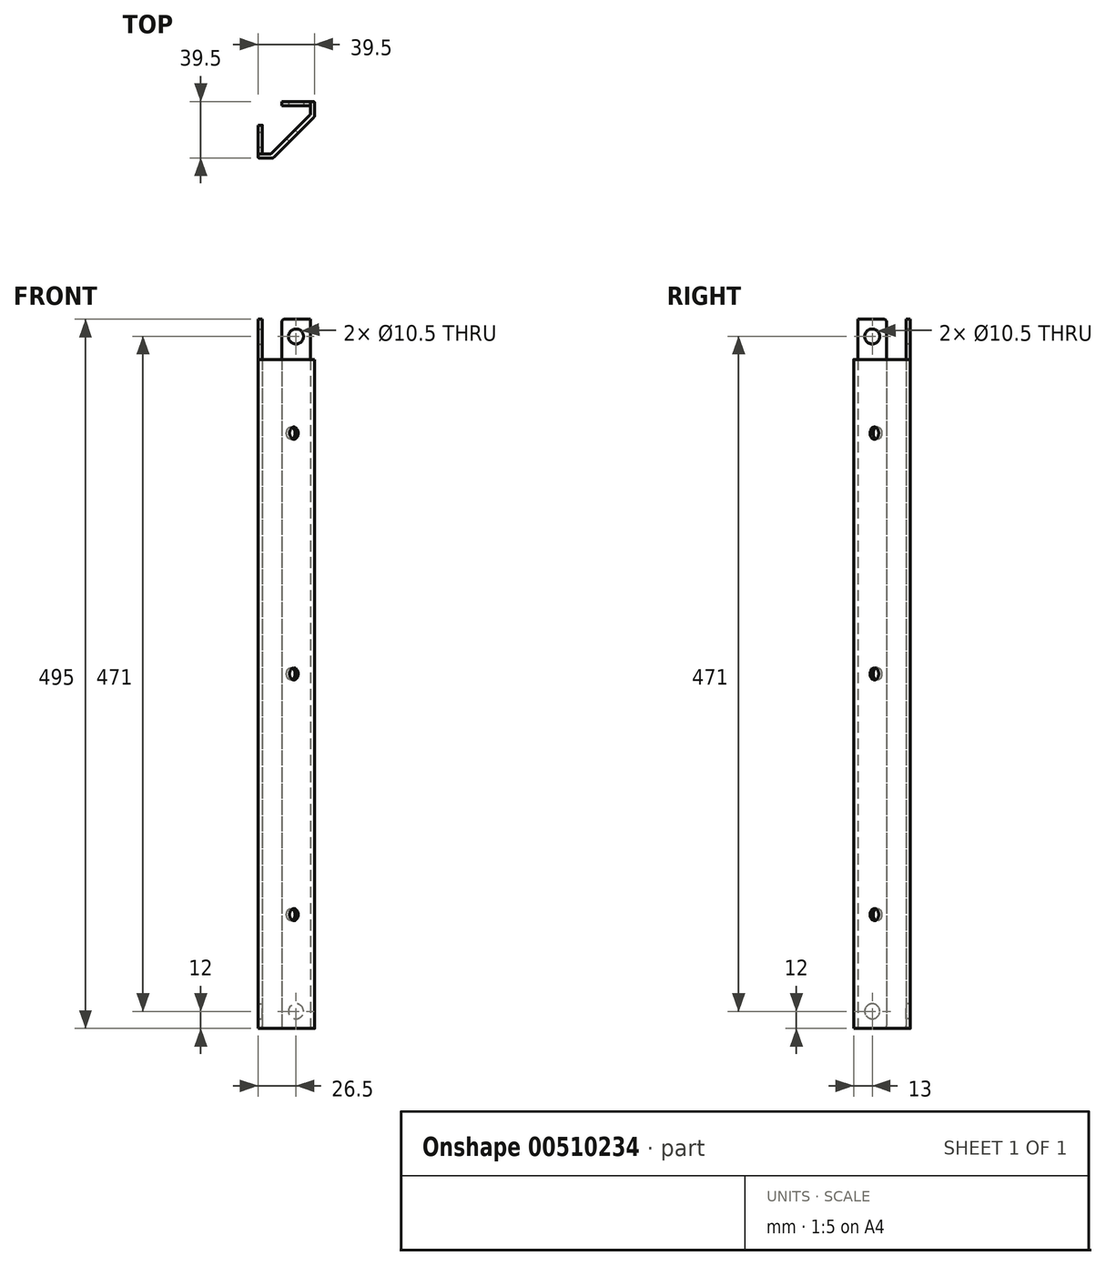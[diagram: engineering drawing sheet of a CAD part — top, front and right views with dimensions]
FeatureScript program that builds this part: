
annotation { "Feature Type Name" : "Feature", "Feature Type Description" : "" }
export const myFeature = defineFeature(function(context is Context, id is Id, definition is map)
    precondition{}
    {
        {
            var Q0;
            Q0=qCreatedBy(makeId("Top.planeOp"),FACE);
            var sketch = newSketch(context, id + "F0", { "sketchPlane" : qUnion([Q0])});
            skLineSegment(sketch, "E0", {"start": v(0, 53.87) * mm, "end": v(0, -58.58) * mm, "construction": true});
            skLineSegment(sketch, "E1", {"start": v(-55.23, 0) * mm, "end": v(53.75, 0) * mm, "construction": true});
            skLineSegment(sketch, "E2.bottom", {"start": v(-19.75, 19.75) * mm, "end": v(19.75, 19.75) * mm, "construction": true});
            skLineSegment(sketch, "E2.top", {"start": v(-19.75, -19.75) * mm, "end": v(19.75, -19.75) * mm, "construction": true});
            skLineSegment(sketch, "E2.left", {"start": v(-19.75, 19.75) * mm, "end": v(-19.75, -19.75) * mm, "construction": true});
            skLineSegment(sketch, "E2.right", {"start": v(19.75, 19.75) * mm, "end": v(19.75, -19.75) * mm, "construction": true});
            skLineSegment(sketch, "E3", {"start": v(-19.75, -19.75) * mm, "end": v(-19.75, 3.25) * mm});
            skLineSegment(sketch, "E4", {"start": v(-19.75, 3.25) * mm, "end": v(-16.75, 3.25) * mm});
            skLineSegment(sketch, "E5", {"start": v(-16.75, 3.25) * mm, "end": v(-16.75, -16.75) * mm});
            skLineSegment(sketch, "E6", {"start": v(-19.75, -19.75) * mm, "end": v(-9.25, -19.75) * mm});
            skLineSegment(sketch, "E7", {"start": v(-9.25, -19.75) * mm, "end": v(19.75, 9.25) * mm, "construction": true});
            skLineSegment(sketch, "E8", {"start": v(-16.75, -6.75) * mm, "end": v(-8.75, -6.75) * mm, "construction": true});
            skLineSegment(sketch, "E9", {"start": v(-8.75, -6.75) * mm, "end": v(-8.75, -15.25) * mm, "construction": true});
            skLineSegment(sketch, "E10.0", {"start": v(-10.5, -16.75) * mm, "end": v(16.75, 10.5) * mm});
            skLineSegment(sketch, "E11", {"start": v(-16.75, -16.75) * mm, "end": v(-10.5, -16.75) * mm});
            skLineSegment(sketch, "E12.0", {"start": v(-10.66, -18.34) * mm, "end": v(18.84, 11.16) * mm, "construction": true});
            skLineSegment(sketch, "E13", {"start": v(-9.25, -19.75) * mm, "end": v(19.75, 9.25) * mm});
            skLineSegment(sketch, "E14", {"start": v(19.75, 9.25) * mm, "end": v(19.75, 19.75) * mm});
            skLineSegment(sketch, "E15", {"start": v(19.75, 19.75) * mm, "end": v(-3.25, 19.75) * mm});
            skLineSegment(sketch, "E16", {"start": v(-3.25, 19.75) * mm, "end": v(-3.25, 16.75) * mm});
            skLineSegment(sketch, "E17", {"start": v(-3.25, 16.75) * mm, "end": v(16.75, 16.75) * mm});
            skLineSegment(sketch, "E18", {"start": v(16.75, 16.75) * mm, "end": v(16.75, 10.5) * mm});
            skSolve(sketch);
        }
        {
            var Q0;
            Q0=qSketchRegion(id+"F0",true);
            extrude(context, id + "F1", {"entities" : qUnion([Q0]), "depth" : 495 * mm, "symmetric" : true});
        }
        {
            var Q0;
            Q0=makeQuery(id+"F1.opExtrude","CAP_FACE",FACE,{"disambiguationData":[OSD([sQuery(id+"F0.wireOp",EDGE,"E3"),sQuery(id+"F0.wireOp",EDGE,"E4"),sQuery(id+"F0.wireOp",EDGE,"E5"),sQuery(id+"F0.wireOp",EDGE,"E6"),sQuery(id+"F0.wireOp",EDGE,"E10.0"),sQuery(id+"F0.wireOp",EDGE,"E11"),sQuery(id+"F0.wireOp",EDGE,"E13"),sQuery(id+"F0.wireOp",EDGE,"E14"),sQuery(id+"F0.wireOp",EDGE,"E15"),sQuery(id+"F0.wireOp",EDGE,"E16"),sQuery(id+"F0.wireOp",EDGE,"E17"),sQuery(id+"F0.wireOp",EDGE,"E18")])],"isStart":false});
            var sketch = newSketch(context, id + "F2", { "sketchPlane" : qUnion([Q0])});
            skLineSegment(sketch, "E19.0", {"start": v(-16.75, -16.75) * mm, "end": v(-10.5, -16.75) * mm});
            skLineSegment(sketch, "E19.1", {"start": v(-10.5, -16.75) * mm, "end": v(16.75, 10.5) * mm});
            skLineSegment(sketch, "E19.2", {"start": v(16.75, 16.75) * mm, "end": v(16.75, 10.5) * mm});
            skLineSegment(sketch, "E19.3", {"start": v(19.75, 9.25) * mm, "end": v(19.75, 19.75) * mm});
            skLineSegment(sketch, "E19.4", {"start": v(-9.25, -19.75) * mm, "end": v(19.75, 9.25) * mm});
            skLineSegment(sketch, "E19.5", {"start": v(-19.75, -19.75) * mm, "end": v(-9.25, -19.75) * mm});
            skLineSegment(sketch, "E20", {"start": v(-16.75, -16.75) * mm, "end": v(-19.75, -16.75) * mm});
            skLineSegment(sketch, "E21", {"start": v(-19.75, -16.75) * mm, "end": v(-19.75, -19.75) * mm});
            skLineSegment(sketch, "E22", {"start": v(16.75, 16.75) * mm, "end": v(16.75, 19.75) * mm});
            skLineSegment(sketch, "E23", {"start": v(16.75, 19.75) * mm, "end": v(19.75, 19.75) * mm});
            skSolve(sketch);
        }
        {
            var Q0;
            Q0=qSketchRegion(id+"F2",true);
            extrude(context, id + "F3", {"entities" : qUnion([Q0]), "operationType" : NewBodyOperationType.REMOVE, "oppositeDirection" : true, "depth" : 28 * mm});
        }
        {
            var Q0;
            Q0=makeQuery(id+"F1.opExtrude","SWEPT_FACE",FACE,{"disambiguationData":[OSD([sQuery(id+"F0.wireOp",EDGE,"E13")])]});
            var sketch = newSketch(context, id + "F4", { "sketchPlane" : qUnion([Q0])});
            skLineSegment(sketch, "E24", {"start": v(0, 219.5) * mm, "end": v(0, -219.5) * mm, "construction": true});
            skLineSegment(sketch, "E25", {"start": v(-20.5, 0) * mm, "end": v(20.5, 0) * mm, "construction": true});
            skCircle(sketch, "E26", {"center": v(0, 168) * mm, "radius": 4.25 * mm});
            skCircle(sketch, "E27.MirrorC", {"center": v(0, -168) * mm, "radius": 4.25 * mm});
            skCircle(sketch, "E28", {"center": v(0, 0) * mm, "radius": 4.25 * mm});
            skSolve(sketch);
        }
        {
            var Q0;
            Q0=qSketchRegion(id+"F4",true);
            extrude(context, id + "F5", {"entities" : qUnion([Q0]), "operationType" : NewBodyOperationType.REMOVE, "oppositeDirection" : true, "depth" : 25 * mm});
        }
        {
            var Q0;
            Q0=makeQuery(id+"F1.opExtrude","SWEPT_FACE",FACE,{"disambiguationData":[OSD([sQuery(id+"F0.wireOp",EDGE,"E5")])]});
            var sketch = newSketch(context, id + "F6", { "sketchPlane" : qUnion([Q0])});
            skLineSegment(sketch, "E29", {"start": v(-6.75, 247.5) * mm, "end": v(-6.75, -247.5) * mm, "construction": true});
            skCircle(sketch, "E30", {"center": v(-6.75, 235.5) * mm, "radius": 5.25 * mm});
            skCircle(sketch, "E31", {"center": v(-6.75, -235.5) * mm, "radius": 5.25 * mm});
            skSolve(sketch);
        }
        {
            var Q0;
            Q0=qSketchRegion(id+"F6",true);
            extrude(context, id + "F7", {"entities" : qUnion([Q0]), "operationType" : NewBodyOperationType.REMOVE, "oppositeDirection" : true, "depth" : 25 * mm});
        }
        {
            var Q0;
            Q0=makeQuery(id+"F1.opExtrude","SWEPT_FACE",FACE,{"disambiguationData":[OSD([sQuery(id+"F0.wireOp",EDGE,"E17")])]});
            var sketch = newSketch(context, id + "F8", { "sketchPlane" : qUnion([Q0])});
            skLineSegment(sketch, "E32", {"start": v(6.75, 247.5) * mm, "end": v(6.75, -247.5) * mm, "construction": true});
            skCircle(sketch, "E33", {"center": v(6.75, 235.5) * mm, "radius": 5.25 * mm});
            skCircle(sketch, "E34", {"center": v(6.75, -235.5) * mm, "radius": 5.25 * mm});
            skSolve(sketch);
        }
        {
            var Q0;
            Q0=qSketchRegion(id+"F8",true);
            extrude(context, id + "F9", {"entities" : qUnion([Q0]), "operationType" : NewBodyOperationType.REMOVE, "oppositeDirection" : true, "depth" : 25 * mm});
        }
        {
            var Q0;
            Q0=makeQuery(id+"F1.opExtrude","SWEPT_EDGE",EDGE,{"disambiguationData":[OSD([sQuery(id+"F0.wireOp",EDGE,"E6"),sQuery(id+"F0.wireOp",EDGE,"E13")])]});
            var Q1;
            Q1=makeQuery(id+"F1.opExtrude","SWEPT_EDGE",EDGE,{"disambiguationData":[OSD([sQuery(id+"F0.wireOp",EDGE,"E13"),sQuery(id+"F0.wireOp",EDGE,"E14")])]});
            var Q2;
            Q2=makeQuery(id+"F3.boolean.opBoolean","COPY",EDGE,{"derivedFrom":makeQuery(id+"F3.opExtrude","CAP_EDGE",EDGE,{"disambiguationData":[OSD([sQuery(id+"F2.wireOp",EDGE,"E19.0"),sQuery(id+"F2.wireOp",EDGE,"E20")])],"isStart":true})});
            var Q3;
            Q3=makeQuery(id+"F1.opExtrude","CAP_EDGE",EDGE,{"disambiguationData":[OSD([sQuery(id+"F0.wireOp",EDGE,"E4")])],"isStart":false});
            var Q4;
            Q4=makeQuery(id+"F1.opExtrude","CAP_EDGE",EDGE,{"disambiguationData":[OSD([sQuery(id+"F0.wireOp",EDGE,"E16")])],"isStart":false});
            var Q5;
            Q5=makeQuery(id+"F3.boolean.opBoolean","COPY",EDGE,{"derivedFrom":makeQuery(id+"F3.opExtrude","CAP_EDGE",EDGE,{"disambiguationData":[OSD([sQuery(id+"F2.wireOp",EDGE,"E19.2"),sQuery(id+"F2.wireOp",EDGE,"E22")])],"isStart":true})});
            var Q6;
            Q6=makeQuery(id+"F1.opExtrude","CAP_EDGE",EDGE,{"disambiguationData":[OSD([sQuery(id+"F0.wireOp",EDGE,"E4")])],"isStart":true});
            var Q7;
            Q7=makeQuery(id+"Fec6EYU1eJzkxKK_1.1.F3.boolean.opBoolean","COPY",EDGE,{"derivedFrom":makeQuery(id+"Fec6EYU1eJzkxKK_1.1.F3.opExtrude","CAP_EDGE",EDGE,{"disambiguationData":[OSD([sQuery(id+"F2.wireOp",EDGE,"E19.0"),sQuery(id+"F2.wireOp",EDGE,"E20")])],"isStart":true})});
            var Q8;
            Q8=makeQuery(id+"F1.opExtrude","CAP_EDGE",EDGE,{"disambiguationData":[OSD([sQuery(id+"F0.wireOp",EDGE,"E16")])],"isStart":true});
            var Q9;
            Q9=makeQuery(id+"Fec6EYU1eJzkxKK_1.1.F3.boolean.opBoolean","COPY",EDGE,{"derivedFrom":makeQuery(id+"Fec6EYU1eJzkxKK_1.1.F3.opExtrude","CAP_EDGE",EDGE,{"disambiguationData":[OSD([sQuery(id+"F2.wireOp",EDGE,"E19.2"),sQuery(id+"F2.wireOp",EDGE,"E22")])],"isStart":true})});
            fillet(context, id + "F10", {"entities" : qUnion([Q0, Q1, Q2, Q3, Q4, Q5, Q6, Q7, Q8, Q9]), "radius" : 2 * mm, "tangentPropagation" : true, "allowEdgeOverflow" : false});
        }
        {
            var Q0;
            Q0=makeQuery(id+"F1.opExtrude","SWEPT_EDGE",EDGE,{"disambiguationData":[OSD([sQuery(id+"F0.wireOp",EDGE,"E10.0"),sQuery(id+"F0.wireOp",EDGE,"E11")])]});
            var Q1;
            Q1=makeQuery(id+"F1.opExtrude","SWEPT_EDGE",EDGE,{"disambiguationData":[OSD([sQuery(id+"F0.wireOp",EDGE,"E10.0"),sQuery(id+"F0.wireOp",EDGE,"E18")])]});
            fillet(context, id + "F11", {"entities" : qUnion([Q0, Q1]), "radius" : 0.5 * mm, "tangentPropagation" : true, "allowEdgeOverflow" : false});
        }
        {
            var Q0;
            Q0=makeQuery(id+"F1.opExtrude","SWEPT_EDGE",EDGE,{"disambiguationData":[OSD([sQuery(id+"F0.wireOp",EDGE,"E3"),sQuery(id+"F0.wireOp",EDGE,"E6")])]});
            var Q1;
            Q1=makeQuery(id+"F1.opExtrude","SWEPT_EDGE",EDGE,{"disambiguationData":[OSD([sQuery(id+"F0.wireOp",EDGE,"E14"),sQuery(id+"F0.wireOp",EDGE,"E15")])]});
            fillet(context, id + "F12", {"entities" : qUnion([Q0, Q1]), "radius" : 1 * mm, "tangentPropagation" : true, "allowEdgeOverflow" : false});
        }
    });
